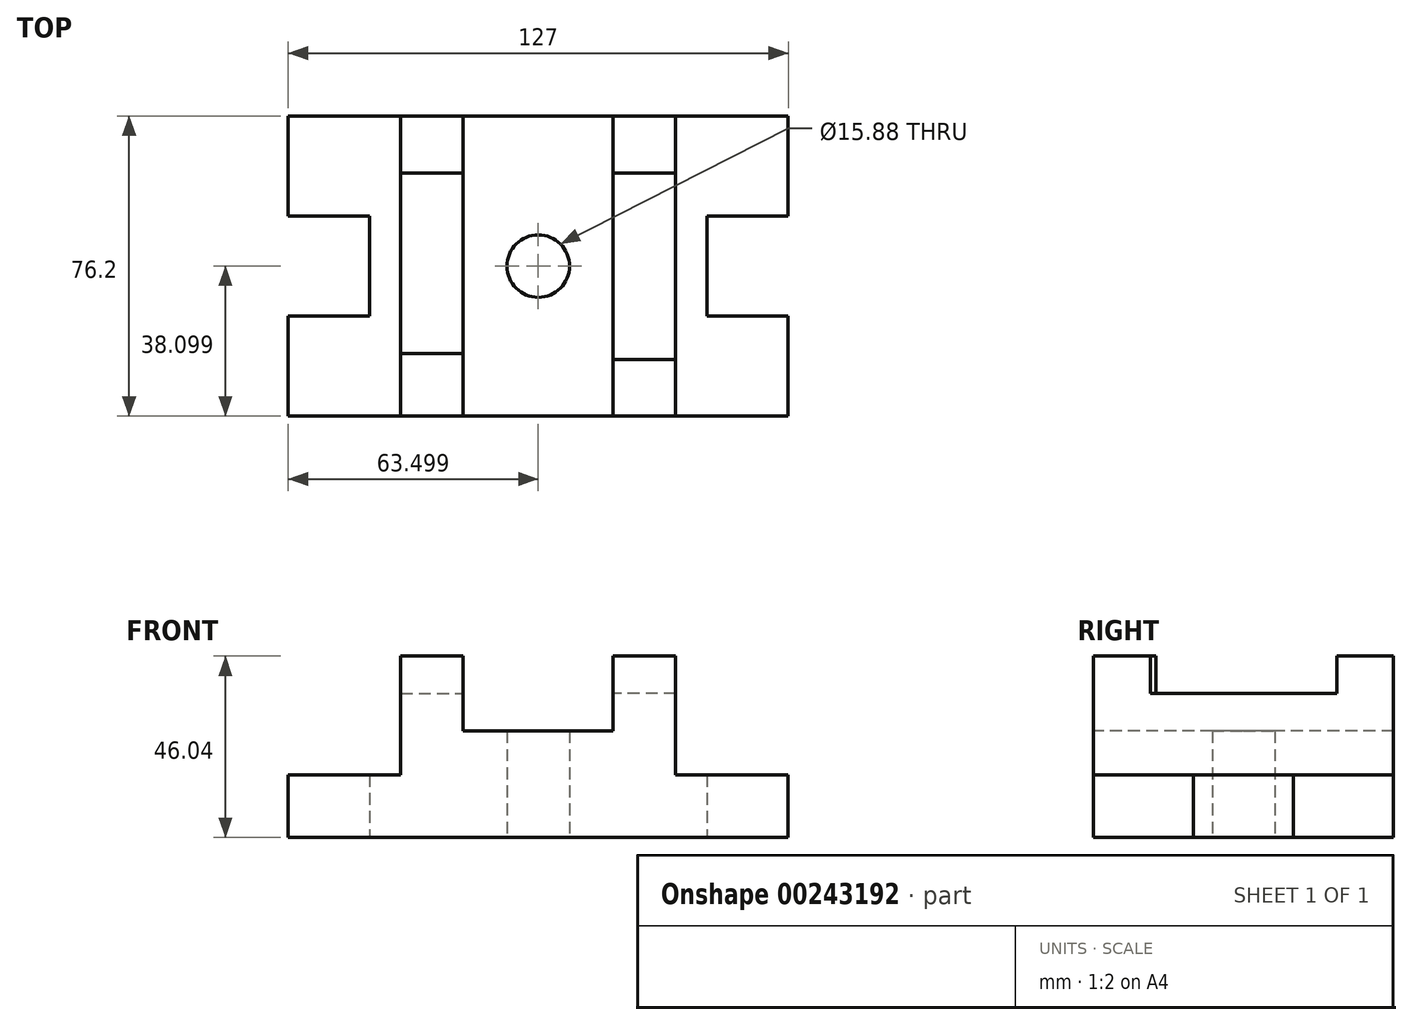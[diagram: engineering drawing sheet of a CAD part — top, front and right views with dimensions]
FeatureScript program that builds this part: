
annotation { "Feature Type Name" : "Feature", "Feature Type Description" : "" }
export const myFeature = defineFeature(function(context is Context, id is Id, definition is map)
    precondition{}
    {
        {
            var Q0;
            Q0=qCreatedBy(makeId("Top.planeOp"),FACE);
            var sketch = newSketch(context, id + "F0", { "sketchPlane" : qUnion([Q0])});
            skLineSegment(sketch, "E0", {"start": v(-114.93, -56.17) * mm, "end": v(139.07, -56.17) * mm});
            skLineSegment(sketch, "E1", {"start": v(-114.93, -56.17) * mm, "end": v(-114.93, -5.37) * mm});
            skLineSegment(sketch, "E2", {"start": v(-114.93, -5.37) * mm, "end": v(-73.66, -5.37) * mm});
            skLineSegment(sketch, "E3", {"start": v(-73.66, -5.37) * mm, "end": v(-73.66, 45.43) * mm});
            skLineSegment(sketch, "E4", {"start": v(-73.66, 45.43) * mm, "end": v(-114.93, 45.43) * mm});
            skLineSegment(sketch, "E5", {"start": v(-114.93, 45.43) * mm, "end": v(-114.93, 96.23) * mm});
            skLineSegment(sketch, "E6", {"start": v(-114.93, 96.23) * mm, "end": v(139.07, 96.23) * mm});
            skLineSegment(sketch, "E7.MirrorCS", {"start": v(97.8, 45.43) * mm, "end": v(139.07, 45.43) * mm});
            skLineSegment(sketch, "E8.MirrorCS", {"start": v(97.8, -5.37) * mm, "end": v(97.8, 45.43) * mm});
            skLineSegment(sketch, "E9.MirrorCS", {"start": v(139.07, 45.43) * mm, "end": v(139.07, 96.23) * mm});
            skLineSegment(sketch, "E10.MirrorCS", {"start": v(139.07, -5.37) * mm, "end": v(97.8, -5.37) * mm});
            skLineSegment(sketch, "E11.MirrorCS", {"start": v(139.07, -56.17) * mm, "end": v(139.07, -5.37) * mm});
            skLineSegment(sketch, "E12", {"start": v(-57.78, 96.23) * mm, "end": v(-57.78, -56.17) * mm});
            skLineSegment(sketch, "E13.MirrorCS", {"start": v(81.92, 96.23) * mm, "end": v(81.92, -56.17) * mm});
            skLineSegment(sketch, "E14", {"start": v(-26.03, 96.23) * mm, "end": v(-26.03, -56.17) * mm});
            skLineSegment(sketch, "E15.MirrorCS", {"start": v(50.17, 96.23) * mm, "end": v(50.17, -56.17) * mm});
            skLineSegment(sketch, "E16", {"start": v(-57.78, -24.42) * mm, "end": v(-26.03, -24.42) * mm});
            skLineSegment(sketch, "E17.MirrorCS", {"start": v(-57.78, 67.4) * mm, "end": v(-26.03, 67.4) * mm});
            skLineSegment(sketch, "E18.MirrorCS", {"start": v(81.92, 67.4) * mm, "end": v(50.17, 67.4) * mm});
            skLineSegment(sketch, "E19.MirrorCS", {"start": v(81.92, -27.34) * mm, "end": v(50.17, -27.34) * mm});
            skCircle(sketch, "E20", {"center": v(12.07, 20.03) * mm, "radius": 15.88 * mm});
            skSolve(sketch);
        }
        {
            var Q0;
            Q0 = qSketchRegion(id + "F0", true);
            extrude(context, id + "F1", {"entities" : qUnion([Q0]), "depth" : 31.75 * mm});
        }
        {
            var Q0;
            {var subQ0=sQuery(id+"F0.wireOp",EDGE,"E16");Q0=makeQuery(id+"F0.imprint","IMPRINT",FACE,{"disambiguationData":[TD([[makeQuery(id+"F0.imprint","IMPRINT",EDGE,{"derivedFrom":subQ0}),1.0]])]});}
            var Q1;
            {var subQ0=sQuery(id+"F0.wireOp",EDGE,"E18.MirrorCS");Q1=makeQuery(id+"F0.imprint","IMPRINT",FACE,{"disambiguationData":[TD([[makeQuery(id+"F0.imprint","IMPRINT",EDGE,{"derivedFrom":subQ0}),1.0]])]});}
            extrude(context, id + "F2", {"entities" : qUnion([Q0, Q1]), "operationType" : NewBodyOperationType.ADD, "depth" : 73.02 * mm});
        }
        {
            var Q0;
            {var subQ5=sQuery(id+"F0.wireOp",EDGE,"E17.MirrorCS");Q0=makeQuery(id+"F0.imprint","IMPRINT",FACE,{"disambiguationData":[TD([[makeQuery(id+"F0.imprint","IMPRINT",EDGE,{"derivedFrom":subQ5}),1.0]])]});}
            var Q1;
            {var subQ5=sQuery(id+"F0.wireOp",EDGE,"E16");Q1=makeQuery(id+"F0.imprint","IMPRINT",FACE,{"disambiguationData":[TD([[makeQuery(id+"F0.imprint","IMPRINT",EDGE,{"derivedFrom":subQ5}),-1.0]])]});}
            var Q2;
            {var subQ5=sQuery(id+"F0.wireOp",EDGE,"E19.MirrorCS");Q2=makeQuery(id+"F0.imprint","IMPRINT",FACE,{"disambiguationData":[TD([[makeQuery(id+"F0.imprint","IMPRINT",EDGE,{"derivedFrom":subQ5}),1.0]])]});}
            var Q3;
            {var subQ5=sQuery(id+"F0.wireOp",EDGE,"E18.MirrorCS");Q3=makeQuery(id+"F0.imprint","IMPRINT",FACE,{"disambiguationData":[TD([[makeQuery(id+"F0.imprint","IMPRINT",EDGE,{"derivedFrom":subQ5}),-1.0]])]});}
            extrude(context, id + "F3", {"entities" : qUnion([Q0, Q1, Q2, Q3]), "operationType" : NewBodyOperationType.ADD, "depth" : 92.07 * mm});
        }
        {
            var Q0;
            {var subQ0=sQuery(id+"F0.wireOp",EDGE,"E13.MirrorCS");var subQ1=sQuery(id+"F0.wireOp",EDGE,"E0");var subQ2=sQuery(id+"F0.wireOp",EDGE,"E15.MirrorCS");var subQ4=sQuery(id+"F0.wireOp",EDGE,"E20");var subQ5=sQuery(id+"F0.wireOp",EDGE,"E19.MirrorCS");var subQ6=sQuery(id+"F0.wireOp",EDGE,"E12");var subQ7=sQuery(id+"F0.wireOp",EDGE,"E14");var subQ9=sQuery(id+"F0.wireOp",EDGE,"E6");var subQ11=sQuery(id+"F0.wireOp",EDGE,"E17.MirrorCS");var subQ13=sQuery(id+"F0.wireOp",EDGE,"E18.MirrorCS");var subQ14=sQuery(id+"F0.wireOp",EDGE,"E16");Q0=makeQuery(id+"F3.boolean.opBoolean","SPLIT",FACE,{"disambiguationData":[TD([makeQuery(id+"F1.opExtrude","SWEPT_FACE",FACE,{"disambiguationData":[OSD([subQ4])]})])],"derivedFrom":makeQuery(id+"F1.opExtrude","CAP_FACE",FACE,{"disambiguationData":[OSD([subQ1,sQuery(id+"F0.wireOp",EDGE,"E1"),sQuery(id+"F0.wireOp",EDGE,"E2"),sQuery(id+"F0.wireOp",EDGE,"E3"),sQuery(id+"F0.wireOp",EDGE,"E4"),sQuery(id+"F0.wireOp",EDGE,"E5"),subQ9,sQuery(id+"F0.wireOp",EDGE,"E7.MirrorCS"),sQuery(id+"F0.wireOp",EDGE,"E8.MirrorCS"),sQuery(id+"F0.wireOp",EDGE,"E9.MirrorCS"),sQuery(id+"F0.wireOp",EDGE,"E10.MirrorCS"),sQuery(id+"F0.wireOp",EDGE,"E11.MirrorCS"),subQ6,subQ0,subQ7,subQ2,subQ14,subQ11,subQ13,subQ5,subQ4])],"isStart":false})});}
            extrude(context, id + "F4", {"entities" : qUnion([Q0]), "operationType" : NewBodyOperationType.ADD, "depth" : 22.22 * mm});
        }
        {
            var Q0;
            Q0=makeQuery(id+"F1.opExtrude","SWEPT_BODY",BODY,{"disambiguationData":[OSD([sQuery(id+"F0.wireOp",EDGE,"E0"),sQuery(id+"F0.wireOp",EDGE,"E1"),sQuery(id+"F0.wireOp",EDGE,"E2"),sQuery(id+"F0.wireOp",EDGE,"E3"),sQuery(id+"F0.wireOp",EDGE,"E4"),sQuery(id+"F0.wireOp",EDGE,"E5"),sQuery(id+"F0.wireOp",EDGE,"E6"),sQuery(id+"F0.wireOp",EDGE,"E7.MirrorCS"),sQuery(id+"F0.wireOp",EDGE,"E8.MirrorCS"),sQuery(id+"F0.wireOp",EDGE,"E9.MirrorCS"),sQuery(id+"F0.wireOp",EDGE,"E10.MirrorCS"),sQuery(id+"F0.wireOp",EDGE,"E11.MirrorCS"),sQuery(id+"F0.wireOp",EDGE,"E12"),sQuery(id+"F0.wireOp",EDGE,"E13.MirrorCS"),sQuery(id+"F0.wireOp",EDGE,"E14"),sQuery(id+"F0.wireOp",EDGE,"E15.MirrorCS"),sQuery(id+"F0.wireOp",EDGE,"E16"),sQuery(id+"F0.wireOp",EDGE,"E17.MirrorCS"),sQuery(id+"F0.wireOp",EDGE,"E18.MirrorCS"),sQuery(id+"F0.wireOp",EDGE,"E19.MirrorCS"),sQuery(id+"F0.wireOp",EDGE,"E20")])]});
            var Q1;
            Q1=makeQuery(id+"F3.opExtrude","CAP_VERTEX",VERTEX,{"disambiguationData":[OSD([sQuery(id+"F0.wireOp",EDGE,"E0"),sQuery(id+"F0.wireOp",EDGE,"E15.MirrorCS")])],"isStart":false});
            transform(context, id + "F5", {"entities" : qUnion([Q0]), "transformType" : TransformType.SCALE_UNIFORMLY, "scale" : .5, "scalePoint" : qUnion([Q1]), "makeCopy" : false});
        }
    });
